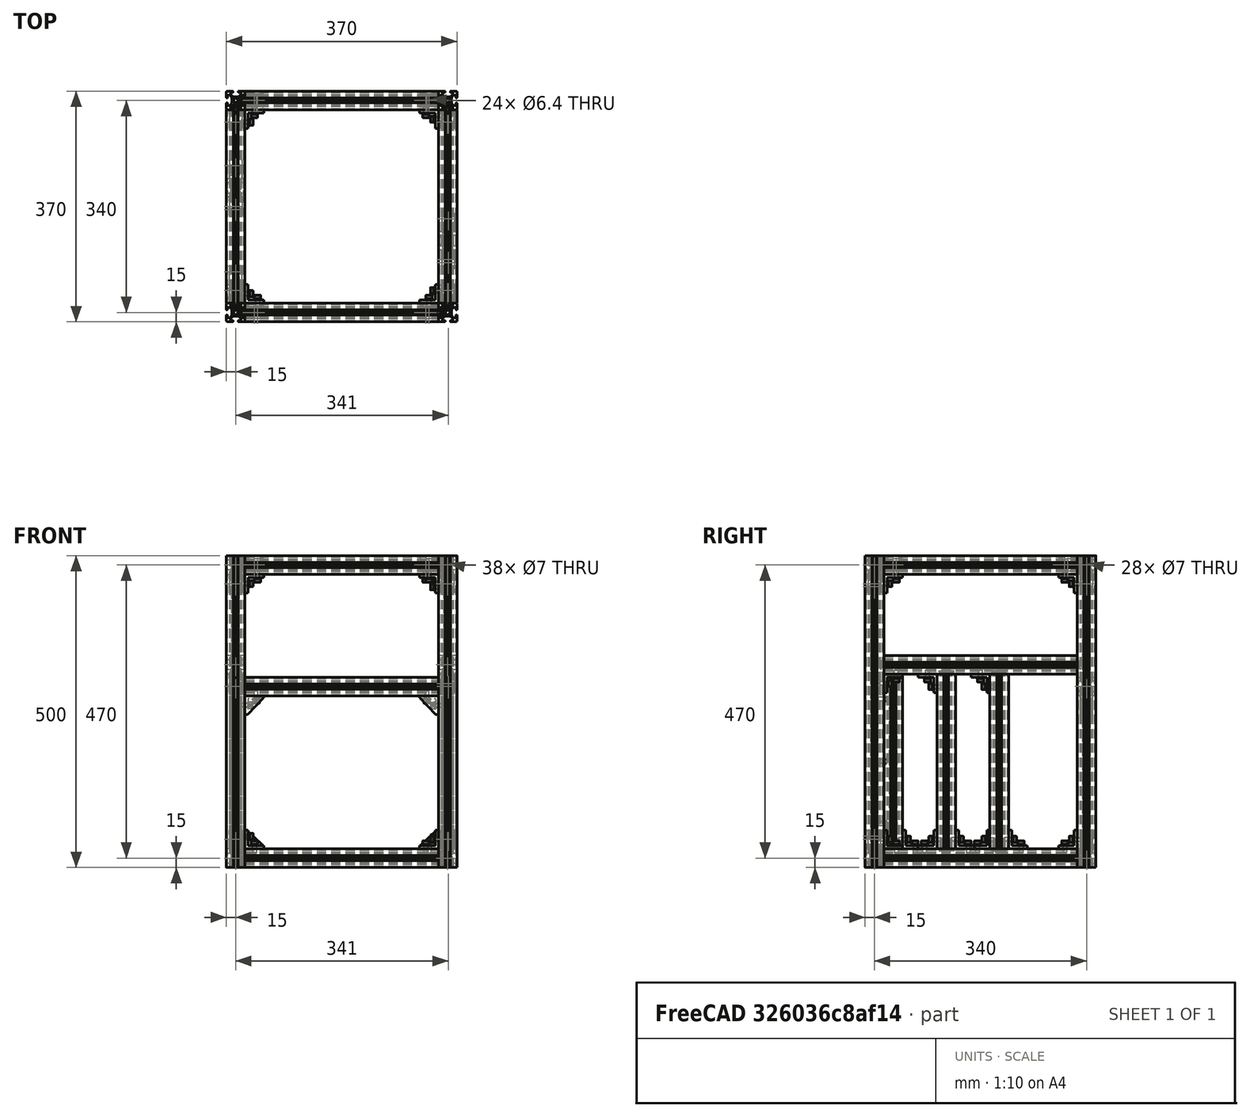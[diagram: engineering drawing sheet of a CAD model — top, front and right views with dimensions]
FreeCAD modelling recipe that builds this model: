
FCSTD DOCUMENT  (FreeCAD 0.19R24291 (Git))
Label: frame-assembly
License: Other
LicenseURL: GPL3
objects: Part::FeaturePython×141, Part::Feature×68, App::Part×4, PartDesign::CoordinateSystem×1
note: 210 computed .brp shape members not serialized (recipe doc carries the construction recipe); baked Part::Feature solids carry a one-line shape summary decoded from their .brp

FEATURE [Part::Feature] Extrude001  label="3030-310mm001-tap"
  Placement = pos=(-155,15,15) rot=(0,1,0;1.5708rad)
  shape: bbox 310 x 30 x 30 mm, 95 faces (baked)
FEATURE [Part::Feature] Extrude002  label="3030-310mm002-tap"
  Placement = pos=(-155,355,15) rot=(0,1,0;1.5708rad)
  shape: bbox 310 x 30 x 30 mm, 95 faces (baked)
FEATURE [Part::Feature] Extrude005  label="3030-310mm003-tap"
  Placement = pos=(170,30,485) rot=(0.57735,-0.57735,-0.57735;4.18879rad)
  shape: bbox 30 x 310 x 30 mm, 95 faces (baked)
FEATURE [Part::Feature] Extrude006  label="3030-310mm004-tap"
  Placement = pos=(-170,30,485) rot=(0.57735,-0.57735,-0.57735;4.18879rad)
  shape: bbox 30 x 310 x 30 mm, 95 faces (baked)
FEATURE [Part::Feature] Extrude007  label="3030-310mm005-tap"
  Placement = pos=(-155,355,485) rot=(0,1,0;1.5708rad)
  shape: bbox 310 x 30 x 30 mm, 95 faces (baked)
FEATURE [Part::Feature] Extrude008  label="3030-310mm006-tap"
  Placement = pos=(-155,15,485) rot=(0,1,0;1.5708rad)
  shape: bbox 310 x 30 x 30 mm, 95 faces (baked)
FEATURE [Part::Feature] Extrude010  label="3030-310mm007-tap"
  Placement = pos=(-155,355,290) rot=(0,1,0;1.5708rad)
  shape: bbox 310 x 30 x 30 mm, 95 faces (baked)
FEATURE [Part::Feature] Extrude002002002002  label="3030-280mm001-tap"
  Placement = pos=(-170,215,30) rot=(0,0,1;0rad)
  shape: bbox 30 x 30 x 280 mm, 95 faces (baked)
FEATURE [Part::Feature] Extrude002002002003  label="3030-280mm002-tap"
  Placement = pos=(170,130,30) rot=(0,0,1;0rad)
  shape: bbox 30 x 30 x 280 mm, 95 faces (baked)
FEATURE [Part::Feature] Cut008004003004014002002003  label="3030-280mm003-tap"
  Placement = pos=(-170,45,30) rot=(0,0,1;0rad)
  shape: bbox 30 x 30 x 280 mm, 137 faces (baked)
FEATURE [Part::Feature] Cut008004003004014002002011  label="3030-310mm008-tap-drill"
  Placement = pos=(-170,30,0) rot=(0,0,1;0rad)
  shape: bbox 30 x 310 x 30 mm, 109 faces (baked)
FEATURE [Part::Feature] Cut008004003004014002002012  label="3030-310mm009-tap-drill"
  Placement = pos=(-170,30,310) rot=(0,0,1;0rad)
  shape: bbox 30 x 310 x 30 mm, 109 faces (baked)
FEATURE [Part::Feature] Cut008004003004014002002013  label="3030-310mm010-tap-drill"
  Placement = pos=(170,30,0) rot=(0,0,1;0rad)
  shape: bbox 30 x 310 x 30 mm, 109 faces (baked)
FEATURE [Part::Feature] Cut008004003004014002002014  label="3030-310mm011-tap-drill"
  Placement = pos=(170,30,310) rot=(0,0,1;0rad)
  shape: bbox 30 x 310 x 30 mm, 109 faces (baked)
FEATURE [Part::Feature] Part__Feature112001022  label="Block-corner-bracket003"
  Placement = pos=(155,355,275) rot=(0.57735,0.57735,-0.57735;4.18879rad)
  shape: bbox 31 x 20 x 31 mm, 71 faces (baked)
FEATURE [Part::Feature] Part__Feature112001023  label="Block-corner-bracket004"
  Placement = pos=(-155,355,275) rot=(0.57735,-0.57735,0.57735;4.18879rad)
  shape: bbox 31 x 20 x 31 mm, 71 faces (baked)
FEATURE [Part::Feature] Part__Feature008  label="L-corner-bracket001"
  Placement = pos=(-155,15,30) rot=(0,0,-1;1.5708rad)
  shape: bbox 30 x 20 x 30 mm, 10 faces (baked)
FEATURE [Part::Feature] Part__Feature112001040  label="L-corner-bracket002"
  Placement = pos=(-155,15,470) rot=(0.57735,-0.57735,0.57735;4.18879rad)
  shape: bbox 30 x 20 x 30 mm, 10 faces (baked)
FEATURE [Part::Feature] Part__Feature112001041  label="L-corner-bracket003"
  Placement = pos=(155,15,470) rot=(0.707107,-0.707107,0;3.14159rad)
  shape: bbox 30 x 20 x 30 mm, 10 faces (baked)
FEATURE [Part::Feature] Part__Feature112001042  label="L-corner-bracket004"
  Placement = pos=(155,15,30) rot=(0.57735,-0.57735,-0.57735;2.0944rad)
  shape: bbox 30 x 20 x 30 mm, 10 faces (baked)
FEATURE [Part::Feature] Part__Feature112001054  label="HCJ_Joint001"
  Placement = pos=(-159,355,290) rot=(0.57735,0.57735,-0.57735;2.0944rad)
  shape: bbox 7.5 x 15 x 24 mm, 29 faces (baked)
FEATURE [Part::Feature] Part__Feature112001055  label="HCJ_Joint002"
  Placement = pos=(160,355,290) rot=(0.57735,-0.57735,-0.57735;4.18879rad)
  shape: bbox 7.5 x 15 x 24 mm, 29 faces (baked)
FEATURE [Part::Feature] Part__Feature112001056  label="HCJ_Joint003"
  Placement = pos=(-159,355,485) rot=(0.57735,0.57735,-0.57735;2.0944rad)
  shape: bbox 7.5 x 15 x 24 mm, 29 faces (baked)
FEATURE [Part::Feature] Part__Feature112001057  label="HCJ_Joint004"
  Placement = pos=(160,355,485) rot=(0.57735,-0.57735,-0.57735;4.18879rad)
  shape: bbox 7.5 x 15 x 24 mm, 29 faces (baked)
FEATURE [Part::Feature] Part__Feature112001058  label="HCJ_Joint005"
  Placement = pos=(-159,355,15) rot=(0.57735,0.57735,-0.57735;2.0944rad)
  shape: bbox 7.5 x 15 x 24 mm, 29 faces (baked)
FEATURE [Part::Feature] Part__Feature112001059  label="HCJ_Joint006"
  Placement = pos=(160,355,15) rot=(0.57735,-0.57735,-0.57735;4.18879rad)
  shape: bbox 7.5 x 15 x 24 mm, 29 faces (baked)
FEATURE [Part::Feature] Part__Feature112001060  label="HCJ_Joint007"
  Placement = pos=(170,344,15) rot=(0.707107,0,-0.707107;3.14159rad)
  shape: bbox 15 x 7.5 x 24 mm, 29 faces (baked)
FEATURE [Part::Feature] Part__Feature112001061  label="HCJ_Joint008"
  Placement = pos=(170,26,15) rot=(0,1,0;1.5708rad)
  shape: bbox 15 x 7.5 x 24 mm, 29 faces (baked)
FEATURE [Part::Feature] Part__Feature112001062  label="HCJ_Joint009"
  Placement = pos=(159,15,15) rot=(0.57735,-0.57735,-0.57735;4.18879rad)
  shape: bbox 7.5 x 15 x 24 mm, 29 faces (baked)
FEATURE [Part::Feature] Part__Feature112001063  label="HCJ_Joint010"
  Placement = pos=(-159,15,15) rot=(0.57735,0.57735,-0.57735;2.0944rad)
  shape: bbox 7.5 x 15 x 24 mm, 29 faces (baked)
FEATURE [Part::Feature] Part__Feature112001064  label="HCJ_Joint011"
  Placement = pos=(-170,26,15) rot=(0,1,0;1.5708rad)
  shape: bbox 15 x 7.5 x 24 mm, 29 faces (baked)
FEATURE [Part::Feature] Part__Feature112001065  label="HCJ_Joint012"
  Placement = pos=(-170,344,485) rot=(0.707107,0,-0.707107;3.14159rad)
  shape: bbox 15 x 7.5 x 24 mm, 29 faces (baked)
FEATURE [Part::Feature] Part__Feature112001066  label="HCJ_Joint013"
  Placement = pos=(170,344,485) rot=(0.707107,0,-0.707107;3.14159rad)
  shape: bbox 15 x 7.5 x 24 mm, 29 faces (baked)
FEATURE [Part::Feature] Part__Feature112001067  label="HCJ_Joint014"
  Placement = pos=(170,26,485) rot=(0,1,0;1.5708rad)
  shape: bbox 15 x 7.5 x 24 mm, 29 faces (baked)
FEATURE [Part::Feature] Part__Feature112001068  label="HCJ_Joint015"
  Placement = pos=(159,15,485) rot=(0.57735,-0.57735,-0.57735;4.18879rad)
  shape: bbox 7.5 x 15 x 24 mm, 29 faces (baked)
FEATURE [Part::Feature] Part__Feature112001069  label="HCJ_Joint016"
  Placement = pos=(-159,15,485) rot=(0.57735,0.57735,-0.57735;2.0944rad)
  shape: bbox 7.5 x 15 x 24 mm, 29 faces (baked)
FEATURE [Part::Feature] Part__Feature112001070  label="HCJ_Joint017"
  Placement = pos=(-170,26,485) rot=(0,1,0;1.5708rad)
  shape: bbox 15 x 7.5 x 24 mm, 29 faces (baked)
FEATURE [Part::Feature] Part__Feature112001071  label="L-corner-bracket005"
  Placement = pos=(-155,30,485) rot=(0,1,0;1.5708rad)
  shape: bbox 30 x 30 x 20 mm, 10 faces (baked)
FEATURE [Part::Feature] Part__Feature112001072  label="L-corner-bracket006"
  Placement = pos=(-155,340,485) rot=(0.57735,0.57735,-0.57735;2.0944rad)
  shape: bbox 30 x 30 x 20 mm, 10 faces (baked)
FEATURE [Part::Feature] Part__Feature112001073  label="L-corner-bracket007"
  Placement = pos=(155,340,485) rot=(0.707107,0,-0.707107;3.14159rad)
  shape: bbox 30 x 30 x 20 mm, 10 faces (baked)
FEATURE [Part::Feature] Part__Feature112001074  label="L-corner-bracket008"
  Placement = pos=(155,30,485) rot=(0.57735,-0.57735,-0.57735;4.18879rad)
  shape: bbox 30 x 30 x 20 mm, 10 faces (baked)
FEATURE [Part::Feature] Part__Feature112001020  label="Block-corner-bracket001"
  Placement = pos=(-155,355,30) rot=(0,0,-1;1.5708rad)
  shape: bbox 31 x 20 x 31 mm, 71 faces (baked)
FEATURE [Part::Feature] Part__Feature112001021  label="Block-corner-bracket002"
  Placement = pos=(155,355,30) rot=(0,0,1;1.5708rad)
  shape: bbox 31 x 20 x 31 mm, 71 faces (baked)
FEATURE [Part::Feature] Part__Feature112001075  label="L-corner-bracket009"
  Placement = pos=(155,355,470) rot=(0.57735,0.57735,-0.57735;4.18879rad)
  shape: bbox 30 x 20 x 30 mm, 10 faces (baked)
FEATURE [Part::Feature] Part__Feature112001078  label="L-corner-bracket011"
  Placement = pos=(170,30,30) rot=(0,0.707107,0.707107;3.14159rad)
  shape: bbox 20 x 30 x 30 mm, 10 faces (baked)
FEATURE [Part::Feature] Part__Feature112001079  label="L-corner-bracket012"
  Placement = pos=(-170,200,30) rot=(1,0,0;1.5708rad)
  shape: bbox 20 x 30 x 30 mm, 10 faces (baked)
FEATURE [Part::Feature] Part__Feature112001080  label="L-corner-bracket013"
  Placement = pos=(171,115,30) rot=(1,0,0;1.5708rad)
  shape: bbox 20 x 30 x 30 mm, 10 faces (baked)
FEATURE [Part::Feature] Part__Feature112001081  label="L-corner-bracket014"
  Placement = pos=(-170,200,310) rot=(1,0,0;3.14159rad)
  shape: bbox 20 x 30 x 30 mm, 10 faces (baked)
FEATURE [Part::Feature] Part__Feature112001082  label="L-corner-bracket016"
  Placement = pos=(171,115,310) rot=(1,0,0;3.14159rad)
  shape: bbox 20 x 30 x 30 mm, 10 faces (baked)
FEATURE [Part::Feature] Part__Feature112001083  label="L-corner-bracket015"
  Placement = pos=(171,30,310) rot=(-1,0,0;1.5708rad)
  shape: bbox 20 x 30 x 30 mm, 10 faces (baked)
FEATURE [Part::Feature] Part__Feature112001084  label="L-corner-bracket018"
  Placement = pos=(171,145,30) rot=(0,0.707107,0.707107;3.14159rad)
  shape: bbox 20 x 30 x 30 mm, 10 faces (baked)
FEATURE [Part::Feature] Part__Feature112001085  label="L-corner-bracket017"
  Placement = pos=(-170,230,30) rot=(0,0.707107,0.707107;3.14159rad)
  shape: bbox 20 x 30 x 30 mm, 10 faces (baked)
FEATURE [Part::Feature] Part__Feature112001086  label="L-corner-bracket020"
  Placement = pos=(-170,60,30) rot=(0,0.707107,0.707107;3.14159rad)
  shape: bbox 20 x 30 x 30 mm, 10 faces (baked)
FEATURE [Part::Feature] Part__Feature112001087  label="HCJ_Joint018"
  Placement = pos=(-170,344,15) rot=(0.707107,0,-0.707107;3.14159rad)
  shape: bbox 15 x 7.5 x 24 mm, 29 faces (baked)
FEATURE [Part::Feature] Part__Feature112001089  label="HCJ_Joint019"
  Placement = pos=(-170,214.5,27) rot=(0.57735,-0.57735,-0.57735;2.0944rad)
  shape: bbox 15 x 24 x 7.5 mm, 29 faces (baked)
FEATURE [Part::Feature] Part__Feature112001090  label="HCJ_Joint020"
  Placement = pos=(-170,214.5,315) rot=(0.57735,0.57735,-0.57735;4.18879rad)
  shape: bbox 15 x 24 x 7.5 mm, 29 faces (baked)
FEATURE [Part::Feature] Part__Feature112001091  label="HCJ_Joint021"
  Placement = pos=(170,130.5,315) rot=(0.57735,0.57735,-0.57735;4.18879rad)
  shape: bbox 15 x 24 x 7.5 mm, 29 faces (baked)
FEATURE [Part::Feature] Part__Feature112001092  label="HCJ_Joint022"
  Placement = pos=(170,130.5,27) rot=(0.57735,-0.57735,-0.57735;2.0944rad)
  shape: bbox 15 x 24 x 7.5 mm, 29 faces (baked)
FEATURE [App::Part] Part049  label="HCJ-joint"
  Group = -> [Part__Feature112001054,Part__Feature112001055,Part__Feature112001056,Part__Feature112001057,Part__Feature112001058,Part__Feature112001059,Part__Feature112001060,Part__Feature112001061,Part__Feature112001062,Part__Feature112001063,Part__Feature112001064,Part__Feature112001065,Part__Feature112001066,Part__Feature112001067,Part__Feature112001068,Part__Feature112001069,Part__Feature112001070,+5 more]
  Origin = -> Origin051
FEATURE [Part::Feature] Part__Feature112001088  label="L-corner-bracket021"
  Placement = pos=(171,340,30) rot=(1,0,0;1.5708rad)
  shape: bbox 20 x 30 x 30 mm, 10 faces (baked)
FEATURE [Part::FeaturePython] Screw  label="M8x20-Screw"  # Fasteners workbench fastener (typed FeaturePython)
  Placement = pos=(170,344,485) rot=(-1,0,0;1.5708rad)
  baseObject = -> Extrude005 [Edge279]
  diameter = 5
  invert = false
  length = 3
  lengthCustom = 20
  matchOuter = false
  offset = 4
  thread = false
  type = 39
FEATURE [Part::FeaturePython] Screw001  label="M8x20-Screw057"  # Fasteners workbench fastener (typed FeaturePython)
  Placement = pos=(159,355,485) rot=(0,1,0;1.5708rad)
  baseObject = -> Extrude007 [Edge279]
  diameter = 5
  invert = false
  length = 3
  lengthCustom = 20
  matchOuter = false
  offset = 4
  thread = false
  type = 39
FEATURE [Part::FeaturePython] Screw002  label="M8x20-Screw007"  # Fasteners workbench fastener (typed FeaturePython)
  Placement = pos=(170,344,325) rot=(-1,0,0;1.5708rad)
  baseObject = -> Cut008004003004014002002014 [Edge190]
  diameter = 5
  invert = false
  length = 3
  lengthCustom = 20
  matchOuter = false
  offset = 4
  thread = false
  type = 39
FEATURE [Part::FeaturePython] Screw003  label="M8x20-Screw008"  # Fasteners workbench fastener (typed FeaturePython)
  Placement = pos=(159,355,290) rot=(0,1,0;1.5708rad)
  baseObject = -> Extrude010 [Edge279]
  diameter = 5
  invert = false
  length = 3
  lengthCustom = 20
  matchOuter = false
  offset = 4
  thread = false
  type = 39
FEATURE [Part::FeaturePython] Screw004  label="M8x20-Screw009"  # Fasteners workbench fastener (typed FeaturePython)
  Placement = pos=(170,344,15) rot=(-1,0,0;1.5708rad)
  baseObject = -> Cut008004003004014002002013 [Edge190]
  diameter = 5
  invert = false
  length = 3
  lengthCustom = 20
  matchOuter = false
  offset = 4
  thread = false
  type = 39
FEATURE [Part::FeaturePython] Screw005  label="M8x20-Screw010"  # Fasteners workbench fastener (typed FeaturePython)
  Placement = pos=(159,355,15) rot=(0,1,0;1.5708rad)
  baseObject = -> Extrude002 [Edge279]
  diameter = 5
  invert = false
  length = 3
  lengthCustom = 20
  matchOuter = false
  offset = 4
  thread = false
  type = 39
FEATURE [Part::FeaturePython] Screw006  label="M8x20-Screw058"  # Fasteners workbench fastener (typed FeaturePython)
  Placement = pos=(-159,355,485) rot=(0,-1,0;1.5708rad)
  baseObject = -> Extrude007 [Edge278]
  diameter = 5
  invert = true
  length = 3
  lengthCustom = 20
  matchOuter = false
  offset = 4
  thread = false
  type = 39
FEATURE [Part::FeaturePython] Screw007  label="M8x20-Screw054"  # Fasteners workbench fastener (typed FeaturePython)
  Placement = pos=(-170,344,485) rot=(-1,0,0;1.5708rad)
  baseObject = -> Extrude006 [Edge279]
  diameter = 5
  invert = false
  length = 3
  lengthCustom = 20
  matchOuter = false
  offset = 4
  thread = false
  type = 39
FEATURE [Part::FeaturePython] Screw008  label="M8x20-Screw019"  # Fasteners workbench fastener (typed FeaturePython)
  Placement = pos=(-170,344,325) rot=(-1,0,0;1.5708rad)
  baseObject = -> Cut008004003004014002002012 [Edge190]
  diameter = 5
  invert = false
  length = 3
  lengthCustom = 20
  matchOuter = false
  offset = 4
  thread = false
  type = 39
FEATURE [Part::FeaturePython] Screw009  label="M8x20-Screw024"  # Fasteners workbench fastener (typed FeaturePython)
  Placement = pos=(-159,355,290) rot=(0,-1,0;1.5708rad)
  baseObject = -> Extrude010 [Edge278]
  diameter = 5
  invert = true
  length = 3
  lengthCustom = 20
  matchOuter = false
  offset = 4
  thread = false
  type = 39
FEATURE [Part::FeaturePython] Screw010  label="M8x20-Screw025"  # Fasteners workbench fastener (typed FeaturePython)
  Placement = pos=(-159,355,15) rot=(0,-1,0;1.5708rad)
  baseObject = -> Extrude002 [Edge278]
  diameter = 5
  invert = true
  length = 3
  lengthCustom = 20
  matchOuter = false
  offset = 4
  thread = false
  type = 39
FEATURE [Part::FeaturePython] Screw011  label="M8x20-Screw022"  # Fasteners workbench fastener (typed FeaturePython)
  Placement = pos=(-170,344,15) rot=(-1,0,0;1.5708rad)
  baseObject = -> Cut008004003004014002002011 [Edge190]
  diameter = 5
  invert = false
  length = 3
  lengthCustom = 20
  matchOuter = false
  offset = 4
  thread = false
  type = 39
FEATURE [Part::FeaturePython] Screw012  label="M8x20-Screw053"  # Fasteners workbench fastener (typed FeaturePython)
  Placement = pos=(-170,26,485) rot=(1,0,0;1.5708rad)
  baseObject = -> Extrude006 [Edge278]
  diameter = 5
  invert = true
  length = 15
  lengthCustom = 20
  matchOuter = false
  offset = 4
  thread = false
  type = 39
FEATURE [Part::FeaturePython] Screw013  label="M8x20-Screw055"  # Fasteners workbench fastener (typed FeaturePython)
  Placement = pos=(-159,15,485) rot=(0,-1,0;1.5708rad)
  baseObject = -> Extrude008 [Edge278]
  diameter = 5
  invert = true
  length = 15
  lengthCustom = 20
  matchOuter = false
  offset = 4
  thread = false
  type = 39
FEATURE [Part::FeaturePython] Screw014  label="M8x20-Screw033"  # Fasteners workbench fastener (typed FeaturePython)
  Placement = pos=(-170,26,325) rot=(1,0,0;1.5708rad)
  baseObject = -> Cut008004003004014002002012 [Edge100]
  diameter = 5
  invert = true
  length = 15
  lengthCustom = 20
  matchOuter = false
  offset = 4
  thread = false
  type = 39
FEATURE [Part::FeaturePython] Screw015  label="M8x20-Screw034"  # Fasteners workbench fastener (typed FeaturePython)
  Placement = pos=(-170,26,15) rot=(1,0,0;1.5708rad)
  baseObject = -> Cut008004003004014002002011 [Edge100]
  diameter = 5
  invert = true
  length = 15
  lengthCustom = 20
  matchOuter = false
  offset = 4
  thread = false
  type = 39
FEATURE [Part::FeaturePython] Screw016  label="M8x20-Screw035"  # Fasteners workbench fastener (typed FeaturePython)
  Placement = pos=(-159,15,15) rot=(0,-1,0;1.5708rad)
  baseObject = -> Extrude001 [Edge278]
  diameter = 5
  invert = true
  length = 15
  lengthCustom = 20
  matchOuter = false
  offset = 4
  thread = false
  type = 39
FEATURE [Part::FeaturePython] Screw017  label="M8x20-Screw056"  # Fasteners workbench fastener (typed FeaturePython)
  Placement = pos=(159,15,485) rot=(0,1,0;1.5708rad)
  baseObject = -> Extrude008 [Edge279]
  diameter = 5
  invert = false
  length = 3
  lengthCustom = 20
  matchOuter = false
  offset = 4
  thread = false
  type = 39
FEATURE [Part::FeaturePython] Screw018  label="M8x20-Screw059"  # Fasteners workbench fastener (typed FeaturePython)
  Placement = pos=(170,26,485) rot=(1,0,0;1.5708rad)
  baseObject = -> Extrude005 [Edge278]
  diameter = 5
  invert = true
  length = 3
  lengthCustom = 20
  matchOuter = false
  offset = 4
  thread = false
  type = 39
FEATURE [Part::FeaturePython] Screw019  label="M8x20-Screw047"  # Fasteners workbench fastener (typed FeaturePython)
  Placement = pos=(170,26,325) rot=(1,0,0;1.5708rad)
  baseObject = -> Cut008004003004014002002014 [Edge100]
  diameter = 5
  invert = true
  length = 3
  lengthCustom = 20
  matchOuter = false
  offset = 4
  thread = false
  type = 39
FEATURE [Part::FeaturePython] Screw020  label="M8x20-Screw044"  # Fasteners workbench fastener (typed FeaturePython)
  Placement = pos=(159,15,15) rot=(0,1,0;1.5708rad)
  baseObject = -> Extrude001 [Edge279]
  diameter = 5
  invert = false
  length = 3
  lengthCustom = 20
  matchOuter = false
  offset = 4
  thread = false
  type = 39
FEATURE [Part::FeaturePython] Screw021  label="M8x20-Screw048"  # Fasteners workbench fastener (typed FeaturePython)
  Placement = pos=(170,26,15) rot=(1,0,0;1.5708rad)
  baseObject = -> Cut008004003004014002002013 [Edge100]
  diameter = 5
  invert = true
  length = 3
  lengthCustom = 20
  matchOuter = false
  offset = 4
  thread = false
  type = 39
FEATURE [Part::FeaturePython] Washer  label="M6-Washer"  # Fasteners workbench fastener (typed FeaturePython)
  Placement = pos=(-150,15,455) rot=(0,1,0;1.5708rad)
  baseObject = -> Part__Feature112001040 [Edge7]
  diameter = 2
  invert = true
  matchOuter = true
  offset = 0
  type = 4
FEATURE [Part::FeaturePython] Washer001  label="M6-Washer119"  # Fasteners workbench fastener (typed FeaturePython)
  Placement = pos=(-135,15,465) rot=(1,0,0;3.14159rad)
  baseObject = -> Part__Feature112001040 [Edge1]
  diameter = 2
  invert = true
  matchOuter = true
  offset = 0
  type = 4
FEATURE [Part::FeaturePython] Washer002  label="M6-Washer114"  # Fasteners workbench fastener (typed FeaturePython)
  Placement = pos=(140,15,465) rot=(1,0,0;3.14159rad)
  baseObject = -> Part__Feature112001041 [Edge7]
  diameter = 2
  invert = true
  matchOuter = true
  offset = 0
  type = 4
FEATURE [Part::FeaturePython] Washer003  label="M6-Washer113"  # Fasteners workbench fastener (typed FeaturePython)
  Placement = pos=(150,15,450) rot=(0,-1,0;1.5708rad)
  baseObject = -> Part__Feature112001041 [Edge1]
  diameter = 2
  invert = true
  matchOuter = true
  offset = 0
  type = 4
FEATURE [Part::FeaturePython] Washer004  label="M6-Washer011"  # Fasteners workbench fastener (typed FeaturePython)
  Placement = pos=(150,15,45) rot=(0,-1,0;1.5708rad)
  baseObject = -> Part__Feature112001042 [Edge7]
  diameter = 2
  invert = true
  matchOuter = true
  offset = 0
  type = 4
FEATURE [Part::FeaturePython] Washer005  label="M6-Washer012"  # Fasteners workbench fastener (typed FeaturePython)
  Placement = pos=(135,15,35) rot=(0,0,1;0rad)
  baseObject = -> Part__Feature112001042 [Edge1]
  diameter = 2
  invert = true
  matchOuter = true
  offset = 0
  type = 4
FEATURE [Part::FeaturePython] Washer006  label="M6-Washer013"  # Fasteners workbench fastener (typed FeaturePython)
  Placement = pos=(-150,15,50) rot=(0,1,0;1.5708rad)
  baseObject = -> Part__Feature008 [Edge4]
  diameter = 2
  invert = true
  matchOuter = true
  offset = 0
  type = 4
FEATURE [Part::FeaturePython] Washer007  label="M6-Washer014"  # Fasteners workbench fastener (typed FeaturePython)
  Placement = pos=(-140,15,35) rot=(0,0,1;0rad)
  baseObject = -> Part__Feature008 [Edge7]
  diameter = 2
  invert = true
  matchOuter = true
  offset = 0
  type = 4
FEATURE [Part::FeaturePython] Washer008  label="M6-Washer027"  # Fasteners workbench fastener (typed FeaturePython)
  Placement = pos=(171,50,305) rot=(1,0,0;3.14159rad)
  baseObject = -> Part__Feature112001083 [Edge1]
  diameter = 2
  invert = true
  matchOuter = true
  offset = 0
  type = 4
FEATURE [Part::FeaturePython] Washer009  label="M6-Washer028"  # Fasteners workbench fastener (typed FeaturePython)
  Placement = pos=(171,35,295) rot=(-1,0,0;1.5708rad)
  baseObject = -> Part__Feature112001083 [Edge7]
  diameter = 2
  invert = true
  matchOuter = true
  offset = 0
  type = 4
FEATURE [Part::FeaturePython] Washer010  label="M6-Washer029"  # Fasteners workbench fastener (typed FeaturePython)
  Placement = pos=(171,100,305) rot=(1,0,0;3.14159rad)
  baseObject = -> Part__Feature112001082 [Edge7]
  diameter = 2
  invert = true
  matchOuter = true
  offset = 0
  type = 4
FEATURE [Part::FeaturePython] Washer011  label="M6-Washer030"  # Fasteners workbench fastener (typed FeaturePython)
  Placement = pos=(171,110,290) rot=(1,0,0;1.5708rad)
  baseObject = -> Part__Feature112001082 [Edge1]
  diameter = 2
  invert = true
  matchOuter = true
  offset = 0
  type = 4
FEATURE [Part::FeaturePython] Washer012  label="M6-Washer031"  # Fasteners workbench fastener (typed FeaturePython)
  Placement = pos=(170,35,45) rot=(-1,0,0;1.5708rad)
  baseObject = -> Part__Feature112001078 [Edge7]
  diameter = 2
  invert = true
  matchOuter = true
  offset = 0
  type = 4
FEATURE [Part::FeaturePython] Washer013  label="M6-Washer032"  # Fasteners workbench fastener (typed FeaturePython)
  Placement = pos=(170,50,35) rot=(0,0,1;0rad)
  baseObject = -> Part__Feature112001078 [Edge1]
  diameter = 2
  invert = true
  matchOuter = true
  offset = 0
  type = 4
FEATURE [Part::FeaturePython] Washer014  label="M6-Washer033"  # Fasteners workbench fastener (typed FeaturePython)
  Placement = pos=(171,95,35) rot=(0,0,1;0rad)
  baseObject = -> Part__Feature112001080 [Edge4]
  diameter = 2
  invert = true
  matchOuter = true
  offset = 0
  type = 4
FEATURE [Part::FeaturePython] Washer015  label="M6-Washer034"  # Fasteners workbench fastener (typed FeaturePython)
  Placement = pos=(171,110,45) rot=(1,0,0;1.5708rad)
  baseObject = -> Part__Feature112001080 [Edge7]
  diameter = 2
  invert = true
  matchOuter = true
  offset = 0
  type = 4
FEATURE [Part::FeaturePython] Washer016  label="M6-Washer035"  # Fasteners workbench fastener (typed FeaturePython)
  Placement = pos=(171,165,35) rot=(0,0,1;0rad)
  baseObject = -> Part__Feature112001084 [Edge4]
  diameter = 2
  invert = true
  matchOuter = true
  offset = 0
  type = 4
FEATURE [Part::FeaturePython] Washer017  label="M6-Washer036"  # Fasteners workbench fastener (typed FeaturePython)
  Placement = pos=(171,150,45) rot=(-1,0,0;1.5708rad)
  baseObject = -> Part__Feature112001084 [Edge7]
  diameter = 2
  invert = true
  matchOuter = true
  offset = 0
  type = 4
FEATURE [Part::FeaturePython] Washer018  label="M6-Washer037"  # Fasteners workbench fastener (typed FeaturePython)
  Placement = pos=(171,320,35) rot=(0,0,1;0rad)
  baseObject = -> Part__Feature112001088 [Edge1]
  diameter = 2
  invert = true
  matchOuter = true
  offset = 0
  type = 4
FEATURE [Part::FeaturePython] Washer019  label="M6-Washer038"  # Fasteners workbench fastener (typed FeaturePython)
  Placement = pos=(171,335,45) rot=(1,0,0;1.5708rad)
  baseObject = -> Part__Feature112001088 [Edge7]
  diameter = 2
  invert = true
  matchOuter = true
  offset = 0
  type = 4
FEATURE [Part::FeaturePython] Washer020  label="M6-Washer039"  # Fasteners workbench fastener (typed FeaturePython)
  Placement = pos=(137,355,270.8) rot=(1,0,0;3.14159rad)
  baseObject = -> Part__Feature112001022 [Edge154]
  diameter = 2
  invert = false
  matchOuter = true
  offset = 0
  type = 4
FEATURE [Part::FeaturePython] Washer021  label="M6-Washer040"  # Fasteners workbench fastener (typed FeaturePython)
  Placement = pos=(150.5,355,260) rot=(0,-1,0;1.5708rad)
  baseObject = -> Part__Feature112001022 [Edge155]
  diameter = 2
  invert = false
  matchOuter = true
  offset = 0
  type = 4
FEATURE [Part::FeaturePython] Washer022  label="M6-Washer041"  # Fasteners workbench fastener (typed FeaturePython)
  Placement = pos=(140,355,34.5) rot=(0,0,1;0rad)
  baseObject = -> Part__Feature112001021 [Edge157]
  diameter = 2
  invert = false
  matchOuter = true
  offset = 0
  type = 4
FEATURE [Part::FeaturePython] Washer023  label="M6-Washer042"  # Fasteners workbench fastener (typed FeaturePython)
  Placement = pos=(150.8,355,48) rot=(0,-1,0;1.5708rad)
  baseObject = -> Part__Feature112001021 [Edge154]
  diameter = 2
  invert = false
  matchOuter = true
  offset = 0
  type = 4
FEATURE [Part::FeaturePython] Washer024  label="M6-Washer043"  # Fasteners workbench fastener (typed FeaturePython)
  Placement = pos=(-140,355,34.5) rot=(0,0,1;0rad)
  baseObject = -> Part__Feature112001020 [Edge155]
  diameter = 2
  invert = false
  matchOuter = true
  offset = 0
  type = 4
FEATURE [Part::FeaturePython] Washer025  label="M6-Washer044"  # Fasteners workbench fastener (typed FeaturePython)
  Placement = pos=(-150.8,355,48) rot=(0,1,0;1.5708rad)
  baseObject = -> Part__Feature112001020 [Edge153]
  diameter = 2
  invert = false
  matchOuter = true
  offset = 0
  type = 4
FEATURE [Part::FeaturePython] Washer026  label="M6-Washer045"  # Fasteners workbench fastener (typed FeaturePython)
  Placement = pos=(-150.5,355,260) rot=(0,1,0;1.5708rad)
  baseObject = -> Part__Feature112001023 [Edge155]
  diameter = 2
  invert = false
  matchOuter = true
  offset = 0
  type = 4
FEATURE [Part::FeaturePython] Washer027  label="M6-Washer046"  # Fasteners workbench fastener (typed FeaturePython)
  Placement = pos=(-137,355,270.8) rot=(1,0,0;3.14159rad)
  baseObject = -> Part__Feature112001023 [Edge153]
  diameter = 2
  invert = false
  matchOuter = true
  offset = 0
  type = 4
FEATURE [Part::FeaturePython] Washer028  label="M6-Washer055"  # Fasteners workbench fastener (typed FeaturePython)
  Placement = pos=(-170,235,45) rot=(-1,0,0;1.5708rad)
  baseObject = -> Part__Feature112001085 [Edge7]
  diameter = 2
  invert = true
  matchOuter = true
  offset = 0
  type = 4
FEATURE [Part::FeaturePython] Washer029  label="M6-Washer056"  # Fasteners workbench fastener (typed FeaturePython)
  Placement = pos=(-170,250,35) rot=(0,0,1;0rad)
  baseObject = -> Part__Feature112001085 [Edge1]
  diameter = 2
  invert = true
  matchOuter = true
  offset = 0
  type = 4
FEATURE [Part::FeaturePython] Washer030  label="M6-Washer057"  # Fasteners workbench fastener (typed FeaturePython)
  Placement = pos=(-170,180,35) rot=(0,0,1;0rad)
  baseObject = -> Part__Feature112001079 [Edge4]
  diameter = 2
  invert = true
  matchOuter = true
  offset = 0
  type = 4
FEATURE [Part::FeaturePython] Washer031  label="M6-Washer058"  # Fasteners workbench fastener (typed FeaturePython)
  Placement = pos=(-170,195,45) rot=(1,0,0;1.5708rad)
  baseObject = -> Part__Feature112001079 [Edge7]
  diameter = 2
  invert = true
  matchOuter = true
  offset = 0
  type = 4
FEATURE [Part::FeaturePython] Washer032  label="M6-Washer059"  # Fasteners workbench fastener (typed FeaturePython)
  Placement = pos=(-170,80,35) rot=(0,0,1;0rad)
  baseObject = -> Part__Feature112001086 [Edge1]
  diameter = 2
  invert = true
  matchOuter = true
  offset = 0
  type = 4
FEATURE [Part::FeaturePython] Washer033  label="M6-Washer060"  # Fasteners workbench fastener (typed FeaturePython)
  Placement = pos=(-170,65,45) rot=(-1,0,0;1.5708rad)
  baseObject = -> Part__Feature112001086 [Edge7]
  diameter = 2
  invert = true
  matchOuter = true
  offset = 0
  type = 4
FEATURE [Part::FeaturePython] Washer034  label="M6-Washer061"  # Fasteners workbench fastener (typed FeaturePython)
  Placement = pos=(-170,195,290) rot=(1,0,0;1.5708rad)
  baseObject = -> Part__Feature112001081 [Edge4]
  diameter = 2
  invert = true
  matchOuter = true
  offset = 0
  type = 4
FEATURE [Part::FeaturePython] Washer035  label="M6-Washer062"  # Fasteners workbench fastener (typed FeaturePython)
  Placement = pos=(-170,185,305) rot=(1,0,0;3.14159rad)
  baseObject = -> Part__Feature112001081 [Edge7]
  diameter = 2
  invert = true
  matchOuter = true
  offset = 0
  type = 4
FEATURE [Part::FeaturePython] Washer036  label="M6-Washer105"  # Fasteners workbench fastener (typed FeaturePython)
  Placement = pos=(135,335,485) rot=(1,0,0;1.5708rad)
  baseObject = -> Part__Feature112001073 [Edge1]
  diameter = 2
  invert = true
  matchOuter = true
  offset = 0
  type = 4
FEATURE [Part::FeaturePython] Washer037  label="M6-Washer106"  # Fasteners workbench fastener (typed FeaturePython)
  Placement = pos=(150,325,485) rot=(0,-1,0;1.5708rad)
  baseObject = -> Part__Feature112001073 [Edge7]
  diameter = 2
  invert = true
  matchOuter = true
  offset = 0
  type = 4
FEATURE [Part::FeaturePython] Washer038  label="M6-Washer112"  # Fasteners workbench fastener (typed FeaturePython)
  Placement = pos=(150,50,485) rot=(0,-1,0;1.5708rad)
  baseObject = -> Part__Feature112001074 [Edge1]
  diameter = 2
  invert = true
  matchOuter = true
  offset = 0
  type = 4
FEATURE [Part::FeaturePython] Washer039  label="M6-Washer111"  # Fasteners workbench fastener (typed FeaturePython)
  Placement = pos=(140,35,485) rot=(-1,0,0;1.5708rad)
  baseObject = -> Part__Feature112001074 [Edge7]
  diameter = 2
  invert = true
  matchOuter = true
  offset = 0
  type = 4
FEATURE [Part::FeaturePython] Washer040  label="M6-Washer116"  # Fasteners workbench fastener (typed FeaturePython)
  Placement = pos=(-135,35,485) rot=(-1,0,0;1.5708rad)
  baseObject = -> Part__Feature112001071 [Edge4]
  diameter = 2
  invert = true
  matchOuter = true
  offset = 0
  type = 4
FEATURE [Part::FeaturePython] Washer041  label="M6-Washer115"  # Fasteners workbench fastener (typed FeaturePython)
  Placement = pos=(-150,45,485) rot=(0,1,0;1.5708rad)
  baseObject = -> Part__Feature112001071 [Edge7]
  diameter = 2
  invert = true
  matchOuter = true
  offset = 0
  type = 4
FEATURE [Part::FeaturePython] Washer042  label="M6-Washer100"  # Fasteners workbench fastener (typed FeaturePython)
  Placement = pos=(-150,320,485) rot=(0,1,0;1.5708rad)
  baseObject = -> Part__Feature112001072 [Edge4]
  diameter = 2
  invert = true
  matchOuter = true
  offset = 0
  type = 4
FEATURE [Part::FeaturePython] Washer043  label="M6-Washer099"  # Fasteners workbench fastener (typed FeaturePython)
  Placement = pos=(-140,335,485) rot=(1,0,0;1.5708rad)
  baseObject = -> Part__Feature112001072 [Edge7]
  diameter = 2
  invert = true
  matchOuter = true
  offset = 0
  type = 4
FEATURE [Part::FeaturePython] Screw022  label="M6x14-Screw007"  # Fasteners workbench fastener (typed FeaturePython)
  Placement = pos=(-148.2,15,50) rot=(0,1,0;1.5708rad)
  baseObject = -> Washer006 [Edge1]
  diameter = 7
  invert = false
  length = 3
  lengthCustom = 14
  matchOuter = true
  offset = 0
  thread = false
  type = 33
FEATURE [Part::FeaturePython] Screw023  label="M6x14-Screw006"  # Fasteners workbench fastener (typed FeaturePython)
  Placement = pos=(-140,15,36.8) rot=(0,0,1;0rad)
  baseObject = -> Washer007 [Edge1]
  diameter = 7
  invert = false
  length = 3
  lengthCustom = 14
  matchOuter = true
  offset = 0
  thread = false
  type = 33
FEATURE [Part::FeaturePython] Screw024  label="M6x14-Screw005"  # Fasteners workbench fastener (typed FeaturePython)
  Placement = pos=(135,15,36.8) rot=(0,0,1;0rad)
  baseObject = -> Washer005 [Edge1]
  diameter = 7
  invert = false
  length = 3
  lengthCustom = 14
  matchOuter = true
  offset = 0
  thread = false
  type = 33
FEATURE [Part::FeaturePython] Screw025  label="M6x14-Screw004"  # Fasteners workbench fastener (typed FeaturePython)
  Placement = pos=(148.2,15,45) rot=(0,-1,0;1.5708rad)
  baseObject = -> Washer004 [Edge1]
  diameter = 7
  invert = false
  length = 3
  lengthCustom = 14
  matchOuter = true
  offset = 0
  thread = false
  type = 33
FEATURE [Part::FeaturePython] Screw026  label="M6x14-Screw074"  # Fasteners workbench fastener (typed FeaturePython)
  Placement = pos=(148.2,15,450) rot=(0,-1,0;1.5708rad)
  baseObject = -> Washer003 [Edge1]
  diameter = 7
  invert = false
  length = 3
  lengthCustom = 14
  matchOuter = true
  offset = 0
  thread = false
  type = 33
FEATURE [Part::FeaturePython] Screw027  label="M6x14-Screw075"  # Fasteners workbench fastener (typed FeaturePython)
  Placement = pos=(140,15,463.2) rot=(1,0,0;3.14159rad)
  baseObject = -> Washer002 [Edge1]
  diameter = 7
  invert = false
  length = 3
  lengthCustom = 14
  matchOuter = true
  offset = 0
  thread = false
  type = 33
FEATURE [Part::FeaturePython] Screw028  label="M6x14-Screw"  # Fasteners workbench fastener (typed FeaturePython)
  Placement = pos=(-135,15,463.2) rot=(1,0,0;3.14159rad)
  baseObject = -> Washer001 [Edge1]
  diameter = 7
  invert = false
  length = 3
  lengthCustom = 14
  matchOuter = true
  offset = 0
  thread = false
  type = 33
FEATURE [Part::FeaturePython] Screw029  label="M6x14-Screw080"  # Fasteners workbench fastener (typed FeaturePython)
  Placement = pos=(-148.2,15,455) rot=(0,1,0;1.5708rad)
  baseObject = -> Washer [Edge1]
  diameter = 7
  invert = false
  length = 3
  lengthCustom = 14
  matchOuter = true
  offset = 0
  thread = false
  type = 33
FEATURE [Part::FeaturePython] Screw030  label="M6x14-Screw015"  # Fasteners workbench fastener (typed FeaturePython)
  Placement = pos=(171,95,36.8) rot=(0,0,1;0rad)
  baseObject = -> Washer014 [Edge1]
  diameter = 7
  invert = false
  length = 3
  lengthCustom = 14
  matchOuter = true
  offset = 0
  thread = false
  type = 33
FEATURE [Part::FeaturePython] Screw031  label="M6x14-Screw014"  # Fasteners workbench fastener (typed FeaturePython)
  Placement = pos=(171,108.2,45) rot=(1,0,0;1.5708rad)
  baseObject = -> Washer015 [Edge1]
  diameter = 7
  invert = false
  length = 3
  lengthCustom = 14
  matchOuter = true
  offset = 0
  thread = false
  type = 33
FEATURE [Part::FeaturePython] Screw032  label="M6x14-Screw012"  # Fasteners workbench fastener (typed FeaturePython)
  Placement = pos=(170,50,36.8) rot=(0,0,1;0rad)
  baseObject = -> Washer013 [Edge1]
  diameter = 7
  invert = false
  length = 3
  lengthCustom = 14
  matchOuter = true
  offset = 0
  thread = false
  type = 33
FEATURE [Part::FeaturePython] Screw033  label="M6x14-Screw013"  # Fasteners workbench fastener (typed FeaturePython)
  Placement = pos=(170,36.8,45) rot=(-1,0,0;1.5708rad)
  baseObject = -> Washer012 [Edge1]
  diameter = 7
  invert = false
  length = 3
  lengthCustom = 14
  matchOuter = true
  offset = 0
  thread = false
  type = 33
FEATURE [Part::FeaturePython] Screw034  label="M6x14-Screw008"  # Fasteners workbench fastener (typed FeaturePython)
  Placement = pos=(171,50,303.2) rot=(1,0,0;3.14159rad)
  baseObject = -> Washer008 [Edge1]
  diameter = 7
  invert = false
  length = 3
  lengthCustom = 14
  matchOuter = true
  offset = 0
  thread = false
  type = 33
FEATURE [Part::FeaturePython] Screw035  label="M6x14-Screw009"  # Fasteners workbench fastener (typed FeaturePython)
  Placement = pos=(171,36.8,295) rot=(-1,0,0;1.5708rad)
  baseObject = -> Washer009 [Edge1]
  diameter = 7
  invert = false
  length = 3
  lengthCustom = 14
  matchOuter = true
  offset = 0
  thread = false
  type = 33
FEATURE [Part::FeaturePython] Screw036  label="M6x14-Screw010"  # Fasteners workbench fastener (typed FeaturePython)
  Placement = pos=(171,108.2,290) rot=(1,0,0;1.5708rad)
  baseObject = -> Washer011 [Edge1]
  diameter = 7
  invert = false
  length = 3
  lengthCustom = 14
  matchOuter = true
  offset = 0
  thread = false
  type = 33
FEATURE [Part::FeaturePython] Screw037  label="M6x14-Screw011"  # Fasteners workbench fastener (typed FeaturePython)
  Placement = pos=(171,100,303.2) rot=(1,0,0;3.14159rad)
  baseObject = -> Washer010 [Edge1]
  diameter = 7
  invert = false
  length = 3
  lengthCustom = 14
  matchOuter = true
  offset = 0
  thread = false
  type = 33
FEATURE [Part::FeaturePython] Screw040  label="M6x14-Screw022"  # Fasteners workbench fastener (typed FeaturePython)
  Placement = pos=(149,355,48) rot=(0,-1,0;1.5708rad)
  baseObject = -> Washer023 [Edge1]
  diameter = 7
  invert = false
  length = 3
  lengthCustom = 14
  matchOuter = true
  offset = 0
  thread = false
  type = 33
FEATURE [Part::FeaturePython] Screw041  label="M6x14-Screw023"  # Fasteners workbench fastener (typed FeaturePython)
  Placement = pos=(140,355,36.3) rot=(0,0,1;0rad)
  baseObject = -> Washer022 [Edge1]
  diameter = 7
  invert = false
  length = 3
  lengthCustom = 14
  matchOuter = true
  offset = 0
  thread = false
  type = 33
FEATURE [Part::FeaturePython] Screw042  label="M6x14-Screw021"  # Fasteners workbench fastener (typed FeaturePython)
  Placement = pos=(148.7,355,260) rot=(0,-1,0;1.5708rad)
  baseObject = -> Washer021 [Edge1]
  diameter = 7
  invert = false
  length = 3
  lengthCustom = 14
  matchOuter = true
  offset = 0
  thread = false
  type = 33
FEATURE [Part::FeaturePython] Screw043  label="M6x14-Screw020"  # Fasteners workbench fastener (typed FeaturePython)
  Placement = pos=(137,355,269) rot=(1,0,0;3.14159rad)
  baseObject = -> Washer020 [Edge1]
  diameter = 7
  invert = false
  length = 3
  lengthCustom = 14
  matchOuter = true
  offset = 0
  thread = false
  type = 33
FEATURE [Part::FeaturePython] Screw044  label="M6x14-Screw027"  # Fasteners workbench fastener (typed FeaturePython)
  Placement = pos=(-137,355,269) rot=(1,0,0;3.14159rad)
  baseObject = -> Washer027 [Edge1]
  diameter = 7
  invert = false
  length = 3
  lengthCustom = 14
  matchOuter = true
  offset = 0
  thread = false
  type = 33
FEATURE [Part::FeaturePython] Screw045  label="M6x14-Screw026"  # Fasteners workbench fastener (typed FeaturePython)
  Placement = pos=(-148.7,355,260) rot=(0,1,0;1.5708rad)
  baseObject = -> Washer026 [Edge1]
  diameter = 7
  invert = false
  length = 3
  lengthCustom = 14
  matchOuter = true
  offset = 0
  thread = false
  type = 33
FEATURE [Part::FeaturePython] Screw046  label="M6x14-Screw025"  # Fasteners workbench fastener (typed FeaturePython)
  Placement = pos=(-149,355,48) rot=(0,1,0;1.5708rad)
  baseObject = -> Washer025 [Edge1]
  diameter = 7
  invert = false
  length = 3
  lengthCustom = 14
  matchOuter = true
  offset = 0
  thread = false
  type = 33
FEATURE [Part::FeaturePython] Screw047  label="M6x14-Screw024"  # Fasteners workbench fastener (typed FeaturePython)
  Placement = pos=(-140,355,36.3) rot=(0,0,1;0rad)
  baseObject = -> Washer024 [Edge1]
  diameter = 7
  invert = false
  length = 3
  lengthCustom = 14
  matchOuter = true
  offset = 0
  thread = false
  type = 33
FEATURE [Part::FeaturePython] Screw048  label="M6x14-Screw028"  # Fasteners workbench fastener (typed FeaturePython)
  Placement = pos=(-170,236.8,45) rot=(-1,0,0;1.5708rad)
  baseObject = -> Washer028 [Edge1]
  diameter = 7
  invert = false
  length = 3
  lengthCustom = 14
  matchOuter = true
  offset = 0
  thread = false
  type = 33
FEATURE [Part::FeaturePython] Screw049  label="M6x14-Screw029"  # Fasteners workbench fastener (typed FeaturePython)
  Placement = pos=(-170,250,36.8) rot=(0,0,1;0rad)
  baseObject = -> Washer029 [Edge1]
  diameter = 7
  invert = false
  length = 3
  lengthCustom = 14
  matchOuter = true
  offset = 0
  thread = false
  type = 33
FEATURE [Part::FeaturePython] Screw050  label="M6x14-Screw030"  # Fasteners workbench fastener (typed FeaturePython)
  Placement = pos=(-170,193.2,45) rot=(1,0,0;1.5708rad)
  baseObject = -> Washer031 [Edge1]
  diameter = 7
  invert = false
  length = 3
  lengthCustom = 14
  matchOuter = true
  offset = 0
  thread = false
  type = 33
FEATURE [Part::FeaturePython] Screw051  label="M6x14-Screw031"  # Fasteners workbench fastener (typed FeaturePython)
  Placement = pos=(-170,180,36.8) rot=(0,0,1;0rad)
  baseObject = -> Washer030 [Edge1]
  diameter = 7
  invert = false
  length = 3
  lengthCustom = 14
  matchOuter = true
  offset = 0
  thread = false
  type = 33
FEATURE [Part::FeaturePython] Screw052  label="M6x14-Screw033"  # Fasteners workbench fastener (typed FeaturePython)
  Placement = pos=(-170,66.8,45) rot=(-1,0,0;1.5708rad)
  baseObject = -> Washer033 [Edge1]
  diameter = 7
  invert = false
  length = 3
  lengthCustom = 14
  matchOuter = true
  offset = 0
  thread = false
  type = 33
FEATURE [Part::FeaturePython] Screw053  label="M6x14-Screw032"  # Fasteners workbench fastener (typed FeaturePython)
  Placement = pos=(-170,80,36.8) rot=(0,0,1;0rad)
  baseObject = -> Washer032 [Edge1]
  diameter = 7
  invert = false
  length = 3
  lengthCustom = 14
  matchOuter = true
  offset = 0
  thread = false
  type = 33
FEATURE [Part::FeaturePython] Screw054  label="M6x14-Screw035"  # Fasteners workbench fastener (typed FeaturePython)
  Placement = pos=(-170,185,303.2) rot=(1,0,0;3.14159rad)
  baseObject = -> Washer035 [Edge1]
  diameter = 7
  invert = false
  length = 3
  lengthCustom = 14
  matchOuter = true
  offset = 0
  thread = false
  type = 33
FEATURE [Part::FeaturePython] Screw055  label="M6x14-Screw034"  # Fasteners workbench fastener (typed FeaturePython)
  Placement = pos=(-170,193.2,290) rot=(1,0,0;1.5708rad)
  baseObject = -> Washer034 [Edge1]
  diameter = 7
  invert = false
  length = 3
  lengthCustom = 14
  matchOuter = true
  offset = 0
  thread = false
  type = 33
FEATURE [Part::FeaturePython] Screw056  label="M6x14-Screw061"  # Fasteners workbench fastener (typed FeaturePython)
  Placement = pos=(-140,333.2,485) rot=(1,0,0;1.5708rad)
  baseObject = -> Washer043 [Edge1]
  diameter = 7
  invert = false
  length = 3
  lengthCustom = 14
  matchOuter = true
  offset = 0
  thread = false
  type = 33
FEATURE [Part::FeaturePython] Screw057  label="M6x14-Screw060"  # Fasteners workbench fastener (typed FeaturePython)
  Placement = pos=(-148.2,320,485) rot=(0,1,0;1.5708rad)
  baseObject = -> Washer042 [Edge1]
  diameter = 7
  invert = false
  length = 3
  lengthCustom = 14
  matchOuter = true
  offset = 0
  thread = false
  type = 33
FEATURE [Part::FeaturePython] Screw058  label="M6x14-Screw066"  # Fasteners workbench fastener (typed FeaturePython)
  Placement = pos=(135,333.2,485) rot=(1,0,0;1.5708rad)
  baseObject = -> Washer036 [Edge1]
  diameter = 7
  invert = false
  length = 3
  lengthCustom = 14
  matchOuter = true
  offset = 0
  thread = false
  type = 33
FEATURE [Part::FeaturePython] Screw059  label="M6x14-Screw067"  # Fasteners workbench fastener (typed FeaturePython)
  Placement = pos=(148.2,325,485) rot=(0,-1,0;1.5708rad)
  baseObject = -> Washer037 [Edge1]
  diameter = 7
  invert = false
  length = 3
  lengthCustom = 14
  matchOuter = true
  offset = 0
  thread = false
  type = 33
FEATURE [Part::FeaturePython] Screw060  label="M6x14-Screw073"  # Fasteners workbench fastener (typed FeaturePython)
  Placement = pos=(148.2,50,485) rot=(0,-1,0;1.5708rad)
  baseObject = -> Washer038 [Edge1]
  diameter = 7
  invert = false
  length = 3
  lengthCustom = 14
  matchOuter = true
  offset = 0
  thread = false
  type = 33
FEATURE [Part::FeaturePython] Screw061  label="M6x14-Screw072"  # Fasteners workbench fastener (typed FeaturePython)
  Placement = pos=(140,36.8,485) rot=(-1,0,0;1.5708rad)
  baseObject = -> Washer039 [Edge1]
  diameter = 7
  invert = false
  length = 3
  lengthCustom = 14
  matchOuter = true
  offset = 0
  thread = false
  type = 33
FEATURE [Part::FeaturePython] Screw062  label="M6x14-Screw076"  # Fasteners workbench fastener (typed FeaturePython)
  Placement = pos=(-135,36.8,485) rot=(-1,0,0;1.5708rad)
  baseObject = -> Washer040 [Edge1]
  diameter = 7
  invert = false
  length = 3
  lengthCustom = 14
  matchOuter = true
  offset = 0
  thread = false
  type = 33
FEATURE [Part::FeaturePython] Screw063  label="M6x14-Screw077"  # Fasteners workbench fastener (typed FeaturePython)
  Placement = pos=(-148.2,45,485) rot=(0,1,0;1.5708rad)
  baseObject = -> Washer041 [Edge1]
  diameter = 7
  invert = false
  length = 3
  lengthCustom = 14
  matchOuter = true
  offset = 0
  thread = false
  type = 33
FEATURE [Part::FeaturePython] Screw064  label="M6x14-Screw017"  # Fasteners workbench fastener (typed FeaturePython)
  Placement = pos=(171,151.8,45) rot=(-1,0,0;1.5708rad)
  baseObject = -> Washer017 [Edge1]
  diameter = 7
  invert = false
  length = 3
  lengthCustom = 14
  matchOuter = true
  offset = 0
  thread = false
  type = 33
FEATURE [Part::FeaturePython] Screw065  label="M6x14-Screw016"  # Fasteners workbench fastener (typed FeaturePython)
  Placement = pos=(171,165,36.8) rot=(0,0,1;0rad)
  baseObject = -> Washer016 [Edge1]
  diameter = 7
  invert = false
  length = 3
  lengthCustom = 14
  matchOuter = true
  offset = 0
  thread = false
  type = 33
FEATURE [Part::FeaturePython] Screw066  label="M6x14-Screw019"  # Fasteners workbench fastener (typed FeaturePython)
  Placement = pos=(171,320,36.8) rot=(0,0,1;0rad)
  baseObject = -> Washer018 [Edge1]
  diameter = 7
  invert = false
  length = 3
  lengthCustom = 14
  matchOuter = true
  offset = 0
  thread = false
  type = 33
FEATURE [Part::FeaturePython] Screw067  label="M6x14-Screw018"  # Fasteners workbench fastener (typed FeaturePython)
  Placement = pos=(171,333.2,45) rot=(1,0,0;1.5708rad)
  baseObject = -> Washer019 [Edge1]
  diameter = 7
  invert = false
  length = 3
  lengthCustom = 14
  matchOuter = true
  offset = 0
  thread = false
  type = 33
FEATURE [Part::FeaturePython] Screw068  label="M6x12-Screw002"  # Fasteners workbench fastener (typed FeaturePython)
  Placement = pos=(-170,32,270) rot=(-1,0,0;1.5708rad)
  baseObject = -> Cut008004003004014002002003 [Edge222]
  diameter = 4
  invert = false
  length = 1
  lengthCustom = 12
  matchOuter = false
  offset = -7
  thread = false
  type = 39
FEATURE [Part::FeaturePython] Screw069  label="M6x12-Screw"  # Fasteners workbench fastener (typed FeaturePython)
  Placement = pos=(-170,32,170) rot=(-1,0,0;1.5708rad)
  baseObject = -> Cut008004003004014002002003 [Edge219]
  diameter = 4
  invert = false
  length = 1
  lengthCustom = 12
  matchOuter = false
  offset = -7
  thread = false
  type = 39
FEATURE [Part::FeaturePython] Screw070  label="M6x12-Screw001"  # Fasteners workbench fastener (typed FeaturePython)
  Placement = pos=(-171.336,32.6146,70) rot=(-0.981627,0.190809,0;1.5708rad)
  baseObject = -> Cut008004003004014002002003 [Edge214]
  diameter = 4
  invert = true
  length = 1
  lengthCustom = 12
  matchOuter = false
  offset = -7
  thread = false
  type = 39
FEATURE [Part::Feature] Part__Feature112001094  label="L-corner-bracket023"
  Placement = pos=(-155,355,470) rot=(0.57735,-0.57735,0.57735;4.18879rad)
  shape: bbox 30 x 20 x 30 mm, 10 faces (baked)
FEATURE [Part::Feature] Part__Feature112001095  label="L-corner-bracket024"
  Placement = pos=(-170,340,470) rot=(0,0.707107,-0.707107;3.14159rad)
  shape: bbox 20 x 30 x 30 mm, 10 faces (baked)
FEATURE [Part::Feature] Part__Feature112001096  label="L-corner-bracket025"
  Placement = pos=(-170,30,470) rot=(-1,0,0;1.5708rad)
  shape: bbox 20 x 30 x 30 mm, 10 faces (baked)
FEATURE [Part::Feature] Part__Feature112001097  label="L-corner-bracket026"
  Placement = pos=(170,340,470) rot=(0,0.707107,-0.707107;3.14159rad)
  shape: bbox 20 x 30 x 30 mm, 10 faces (baked)
FEATURE [Part::Feature] Part__Feature112001098  label="L-corner-bracket027"
  Placement = pos=(170,30,470) rot=(-1,0,0;1.5708rad)
  shape: bbox 20 x 30 x 30 mm, 10 faces (baked)
FEATURE [Part::FeaturePython] Washer044  label="M6-Washer110"  # Fasteners workbench fastener (typed FeaturePython)
  Placement = pos=(170,50,465) rot=(1,0,0;3.14159rad)
  baseObject = -> Part__Feature112001098 [Edge1]
  diameter = 2
  invert = true
  matchOuter = true
  offset = 0
  type = 4
FEATURE [Part::FeaturePython] Washer045  label="M6-Washer109"  # Fasteners workbench fastener (typed FeaturePython)
  Placement = pos=(170,35,455) rot=(-1,0,0;1.5708rad)
  baseObject = -> Part__Feature112001098 [Edge7]
  diameter = 2
  invert = true
  matchOuter = true
  offset = 0
  type = 4
FEATURE [Part::FeaturePython] Washer046  label="M6-Washer108"  # Fasteners workbench fastener (typed FeaturePython)
  Placement = pos=(170,320,465) rot=(1,0,0;3.14159rad)
  baseObject = -> Part__Feature112001097 [Edge1]
  diameter = 2
  invert = true
  matchOuter = true
  offset = 0
  type = 4
FEATURE [Part::FeaturePython] Washer047  label="M6-Washer107"  # Fasteners workbench fastener (typed FeaturePython)
  Placement = pos=(170,335,455) rot=(1,0,0;1.5708rad)
  baseObject = -> Part__Feature112001097 [Edge7]
  diameter = 2
  invert = true
  matchOuter = true
  offset = 0
  type = 4
FEATURE [Part::FeaturePython] Washer048  label="M6-Washer103"  # Fasteners workbench fastener (typed FeaturePython)
  Placement = pos=(135,355,465) rot=(1,0,0;3.14159rad)
  baseObject = -> Part__Feature112001075 [Edge1]
  diameter = 2
  invert = true
  matchOuter = true
  offset = 0
  type = 4
FEATURE [Part::FeaturePython] Washer049  label="M6-Washer104"  # Fasteners workbench fastener (typed FeaturePython)
  Placement = pos=(150,355,455) rot=(0,-1,0;1.5708rad)
  baseObject = -> Part__Feature112001075 [Edge7]
  diameter = 2
  invert = true
  matchOuter = true
  offset = 0
  type = 4
FEATURE [Part::FeaturePython] Washer050  label="M6-Washer102"  # Fasteners workbench fastener (typed FeaturePython)
  Placement = pos=(-135,355,465) rot=(1,0,0;3.14159rad)
  baseObject = -> Part__Feature112001094 [Edge1]
  diameter = 2
  invert = true
  matchOuter = true
  offset = 0
  type = 4
FEATURE [Part::FeaturePython] Washer051  label="M6-Washer101"  # Fasteners workbench fastener (typed FeaturePython)
  Placement = pos=(-150,355,455) rot=(0,1,0;1.5708rad)
  baseObject = -> Part__Feature112001094 [Edge7]
  diameter = 2
  invert = true
  matchOuter = true
  offset = 0
  type = 4
FEATURE [Part::FeaturePython] Washer052  label="M6-Washer097"  # Fasteners workbench fastener (typed FeaturePython)
  Placement = pos=(-170,320,465) rot=(1,0,0;3.14159rad)
  baseObject = -> Part__Feature112001095 [Edge4]
  diameter = 2
  invert = true
  matchOuter = true
  offset = 0
  type = 4
FEATURE [Part::FeaturePython] Washer053  label="M6-Washer098"  # Fasteners workbench fastener (typed FeaturePython)
  Placement = pos=(-170,335,455) rot=(1,0,0;1.5708rad)
  baseObject = -> Part__Feature112001095 [Edge7]
  diameter = 2
  invert = true
  matchOuter = true
  offset = 0
  type = 4
FEATURE [Part::FeaturePython] Washer054  label="M6-Washer118"  # Fasteners workbench fastener (typed FeaturePython)
  Placement = pos=(-170,50,465) rot=(1,0,0;3.14159rad)
  baseObject = -> Part__Feature112001096 [Edge1]
  diameter = 2
  invert = true
  matchOuter = true
  offset = 0
  type = 4
FEATURE [Part::FeaturePython] Washer055  label="M6-Washer117"  # Fasteners workbench fastener (typed FeaturePython)
  Placement = pos=(-170,35,455) rot=(-1,0,0;1.5708rad)
  baseObject = -> Part__Feature112001096 [Edge7]
  diameter = 2
  invert = true
  matchOuter = true
  offset = 0
  type = 4
FEATURE [Part::FeaturePython] Screw071  label="M6x14-Screw079"  # Fasteners workbench fastener (typed FeaturePython)
  Placement = pos=(-170,50,463.2) rot=(1,0,0;3.14159rad)
  baseObject = -> Washer054 [Edge1]
  diameter = 7
  invert = false
  length = 3
  lengthCustom = 14
  matchOuter = true
  offset = 0
  thread = false
  type = 33
FEATURE [Part::FeaturePython] Screw072  label="M6x14-Screw078"  # Fasteners workbench fastener (typed FeaturePython)
  Placement = pos=(-170,36.8,455) rot=(-1,0,0;1.5708rad)
  baseObject = -> Washer055 [Edge1]
  diameter = 7
  invert = false
  length = 3
  lengthCustom = 14
  matchOuter = true
  offset = 0
  thread = false
  type = 33
FEATURE [Part::FeaturePython] Screw073  label="M6x14-Screw059"  # Fasteners workbench fastener (typed FeaturePython)
  Placement = pos=(-170,333.2,455) rot=(1,0,0;1.5708rad)
  baseObject = -> Washer053 [Edge1]
  diameter = 7
  invert = false
  length = 3
  lengthCustom = 14
  matchOuter = true
  offset = 0
  thread = false
  type = 33
FEATURE [Part::FeaturePython] Screw074  label="M6x14-Screw058"  # Fasteners workbench fastener (typed FeaturePython)
  Placement = pos=(-170,320,463.2) rot=(1,0,0;3.14159rad)
  baseObject = -> Washer052 [Edge1]
  diameter = 7
  invert = false
  length = 3
  lengthCustom = 14
  matchOuter = true
  offset = 0
  thread = false
  type = 33
FEATURE [Part::FeaturePython] Screw075  label="M6x14-Screw064"  # Fasteners workbench fastener (typed FeaturePython)
  Placement = pos=(135,355,463.2) rot=(1,0,0;3.14159rad)
  baseObject = -> Washer048 [Edge1]
  diameter = 7
  invert = false
  length = 3
  lengthCustom = 14
  matchOuter = true
  offset = 0
  thread = false
  type = 33
FEATURE [Part::FeaturePython] Screw076  label="M6x14-Screw065"  # Fasteners workbench fastener (typed FeaturePython)
  Placement = pos=(148.2,355,455) rot=(0,-1,0;1.5708rad)
  baseObject = -> Washer049 [Edge1]
  diameter = 7
  invert = false
  length = 3
  lengthCustom = 14
  matchOuter = true
  offset = 0
  thread = false
  type = 33
FEATURE [Part::FeaturePython] Screw077  label="M6x14-Screw063"  # Fasteners workbench fastener (typed FeaturePython)
  Placement = pos=(-135,355,463.2) rot=(1,0,0;3.14159rad)
  baseObject = -> Washer050 [Edge1]
  diameter = 7
  invert = false
  length = 3
  lengthCustom = 14
  matchOuter = true
  offset = 0
  thread = false
  type = 33
FEATURE [Part::FeaturePython] Screw078  label="M6x14-Screw062"  # Fasteners workbench fastener (typed FeaturePython)
  Placement = pos=(-148.2,355,455) rot=(0,1,0;1.5708rad)
  baseObject = -> Washer051 [Edge1]
  diameter = 7
  invert = false
  length = 3
  lengthCustom = 14
  matchOuter = true
  offset = 0
  thread = false
  type = 33
FEATURE [Part::FeaturePython] Screw079  label="M6x14-Screw069"  # Fasteners workbench fastener (typed FeaturePython)
  Placement = pos=(170,320,463.2) rot=(1,0,0;3.14159rad)
  baseObject = -> Washer046 [Edge1]
  diameter = 7
  invert = false
  length = 3
  lengthCustom = 14
  matchOuter = true
  offset = 0
  thread = false
  type = 33
FEATURE [Part::FeaturePython] Screw080  label="M6x14-Screw068"  # Fasteners workbench fastener (typed FeaturePython)
  Placement = pos=(170,333.2,455) rot=(1,0,0;1.5708rad)
  baseObject = -> Washer047 [Edge1]
  diameter = 7
  invert = false
  length = 3
  lengthCustom = 14
  matchOuter = true
  offset = 0
  thread = false
  type = 33
FEATURE [Part::FeaturePython] Screw081  label="M6x14-Screw071"  # Fasteners workbench fastener (typed FeaturePython)
  Placement = pos=(170,50,463.2) rot=(1,0,0;3.14159rad)
  baseObject = -> Washer044 [Edge1]
  diameter = 7
  invert = false
  length = 3
  lengthCustom = 14
  matchOuter = true
  offset = 0
  thread = false
  type = 33
FEATURE [Part::FeaturePython] Screw082  label="M6x14-Screw070"  # Fasteners workbench fastener (typed FeaturePython)
  Placement = pos=(170,36.8,455) rot=(-1,0,0;1.5708rad)
  baseObject = -> Washer045 [Edge1]
  diameter = 7
  invert = false
  length = 3
  lengthCustom = 14
  matchOuter = true
  offset = 0
  thread = false
  type = 33
FEATURE [App::Part] Part048  label="frame-bracket"
  Group = -> [Part049,Washer001,Screw028,Screw029,Part__Feature112001040,Washer,Screw026,Screw027,Washer003,Part__Feature112001041,Washer002,Screw025,Screw024,Washer005,Part__Feature112001042,Washer004,Screw023,Screw022,Washer007,Part__Feature008,Washer006,Screw034,Washer009,Screw035,Part__Feature112001083,Washer008,Washer011,Screw036,Screw037,Part__Feature112001082,Washer010,Screw032,Screw033,Washer013,+107 more]
  Origin = -> Origin050
FEATURE [Part::FeaturePython] Screw083  label="M8x20-Screw049"  # Fasteners workbench fastener (typed FeaturePython)
  Placement = pos=(170,130.5,315) rot=(0,0,1;0rad)
  baseObject = -> Part__Feature112001091 [Edge1]
  diameter = 5
  invert = false
  length = 3
  lengthCustom = 20
  matchOuter = true
  offset = 0
  thread = false
  type = 40
FEATURE [Part::FeaturePython] Screw084  label="M8x20-Screw050"  # Fasteners workbench fastener (typed FeaturePython)
  Placement = pos=(-170,214.5,315) rot=(0,0,1;0rad)
  baseObject = -> Part__Feature112001090 [Edge1]
  diameter = 5
  invert = false
  length = 3
  lengthCustom = 20
  matchOuter = true
  offset = 0
  thread = false
  type = 40
FEATURE [Part::FeaturePython] Screw085  label="M8x20-Screw051"  # Fasteners workbench fastener (typed FeaturePython)
  Placement = pos=(-170,214.5,27) rot=(1,0,0;3.14159rad)
  baseObject = -> Part__Feature112001089 [Edge1]
  diameter = 5
  invert = false
  length = 3
  lengthCustom = 20
  matchOuter = true
  offset = 0
  thread = false
  type = 40
FEATURE [Part::FeaturePython] Screw086  label="M8x20-Screw052"  # Fasteners workbench fastener (typed FeaturePython)
  Placement = pos=(170,130.5,27) rot=(1,0,0;3.14159rad)
  baseObject = -> Part__Feature112001092 [Edge1]
  diameter = 5
  invert = false
  length = 3
  lengthCustom = 20
  matchOuter = true
  offset = 0
  thread = false
  type = 40
FEATURE [PartDesign::CoordinateSystem] LCS_main_frame  label="LCS_main-frame"
  AttacherType = Attacher::AttachEngine3D
FEATURE [Part::Feature] Cut002001  label="3030-500mm-front001-tap-drill"
  Placement = pos=(-170,15,0) rot=(0,0,1;0rad)
  shape: bbox 30 x 30 x 500 mm, 167 faces (baked)
FEATURE [Part::Feature] Cut003001  label="3030-500mm-back001-tap-drill"
  Placement = pos=(-170,355,0) rot=(0,0,1;0rad)
  shape: bbox 30 x 30 x 500 mm, 181 faces (baked)
FEATURE [Part::Feature] Cut008004003004014002002015  label="3030-500mm-front002-tap-drill"
  Placement = pos=(170,15,0) rot=(0,0,1;0rad)
  shape: bbox 30 x 30 x 500 mm, 167 faces (baked)
FEATURE [Part::Feature] Cut008004003004014002002016  label="3030-500mm-back002-tap-drill"
  Placement = pos=(170,355,0) rot=(0,0,1;0rad)
  shape: bbox 30 x 30 x 500 mm, 181 faces (baked)
FEATURE [App::Part] Part  label="extrusion"
  Group = -> [Extrude002002002002,Extrude002002002003,Cut008004003004014002002003,Screw020,Screw016,Extrude001,Screw013,Screw017,Extrude008,Screw015,Screw011,Cut008004003004014002002011,Screw008,Screw014,Cut008004003004014002002012,Screw012,Screw007,Extrude006,Screw005,Screw010,Extrude002,Screw004,Screw021,Cut008004003004014002002013,Screw003,Screw009,Extrude010,Screw019,Screw002,Cut008004003004014002002014,+17 more]
  Origin = -> Origin
FEATURE [App::Part] Part054  label="main-frame"
  Group = -> [Part048,Part,LCS_main_frame]
  Origin = -> Origin056
